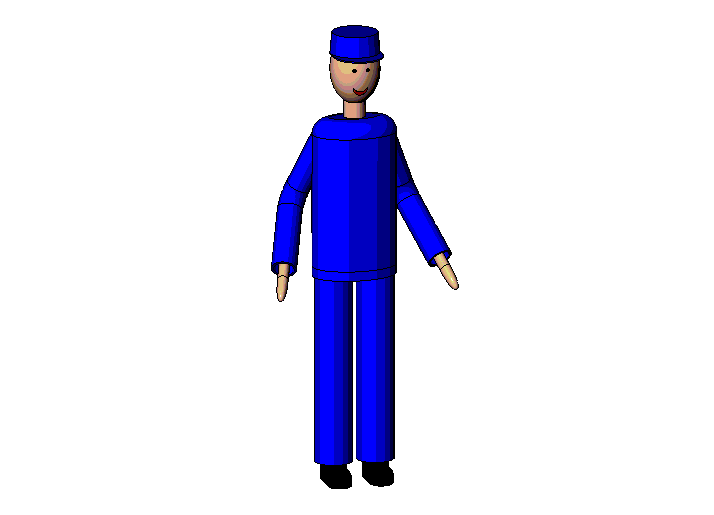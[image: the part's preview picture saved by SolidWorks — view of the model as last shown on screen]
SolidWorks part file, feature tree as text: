
SOLIDWORKS PART (.sldprt)
format: sldprt  version: not decoded by parser v0  size: 772,096 bytes
history: native  units: mm
features: sketch x14, plane x11, extrude x10, mirror x4, fillet x4, revolve x1, sweep x1, cut_extrude x1, dome x1 (+7 scaffold rows collapsed)
feature tree (54):
  scaffold x7  (default folders/planes/origin — collapsed)
  plane  "Ebene1"
  plane  "Ebene2"
  plane  "Ebene3"
  plane  "Ebene4"  Offset=90.001mm
  plane  "Ebene5"  Offset=110mm
  plane  "Ebene6"  Offset=1520.001mm
  plane  "Ebene7"
  plane  "Ebene8"  Offset=400mm
  plane  "Ebene10"  Offset=1840mm
  sketch  "Skizze1"  dims[c1.D1=~14.612521mm c2.D1=90.0deg c3.D1=100.0mm c3.D2=200.0mm c3.D3=150.0mm]
  extrude  "Fuss_rechts"  Depth=75mm
  sketch  "Skizze3"  dims[D1=100.0mm]
  extrude  "Schuh_rechts"  Depth=50mm
  sketch  "Skizze4"  dims[D1=160.0mm]
  extrude  "Bein_rechts"  Depth=800mm
  sketch  "Skizze6"  dims[c1.D1=250.0mm c1.D2=370.0mm c1.D3=95.0mm c2.D2=10.0mm c2.D3=340.0mm c2.D4=125.0mm c2.D5=170.0mm c2.D6=80.0mm c2.D7=125.0mm c2.D8=185.0mm c2.D9=340.0mm c2.D10=~257.039004mm c2.D11=250.0mm c2.D1=10.0mm c3.D2=120.0mm c3.D3=90.0mm]
  extrude  "Torso"  Depth=640mm
  mirror  "Bein_links"
  mirror  "Schuh_links"
  mirror  "Fuss_links"
  fillet  "Schuhe_oben"  Radius=40mm
  fillet  "Schuhe_hinten"  Radius=30mm
  fillet  "Sohle"  Radius=5mm
  sketch  "Skizze8"  dims[D1=90.0mm]
  extrude  "Hals"  Depth=110mm
  sketch  "Skizze10"  dims[D1=60.0mm D2=300.0mm D3=210.0mm D4=1775.0mm D5=~1776.013795mm]
  revolve  "Kopf"  Angle=360deg
  fillet  "Schulter"  Radius=70mm
  sketch  "Skizze13"  dims[c1.D1=105.0mm c1.D2=130.0mm c1.D3=130.0mm c2.D2=~933.553335mm c2.D3=~934.044271mm]
  sketch  "Skizze24"  dims[D1=210.0mm]
  extrude  "Muetze"  Depth=92mm
  sketch  "Skizze27"  dims[D1=180.0mm D2=110.0mm]
  extrude  "Muetzenschirm"  Depth=5mm
  plane  "Ebene11"
  sketch  "Skizze28"
  sweep  "Aermel_links"
  sketch  "Skizze29"  dims[D1=10.0mm]
  cut_extrude  "Aermel_innen_links"  Depth=200mm
  sketch  "Skizze30"  dims[D1=20.0mm]
  extrude  "Arm_links"  Depth=250mm
  dome  "Hand_links"
  mirror  "Arm_rechts"
  plane  "Ebene12"  Offset=130mm
  sketch  "Skizze31"  dims[D1=15.0mm D2=15.0mm]
  extrude  "Mund"  Depth=1mm
  sketch  "Skizze32"  dims[D1=15.0mm D2=15.0mm D3=50.0mm D4=~59.297348mm]
  extrude  "Augen"  Depth=1mm
decode coverage: 29 of 36 modeling features carry decoded parameters
note: ~ marks probable driven/reference dimensions
note: suppression state not decoded; provenance and decode notes live in map.json
